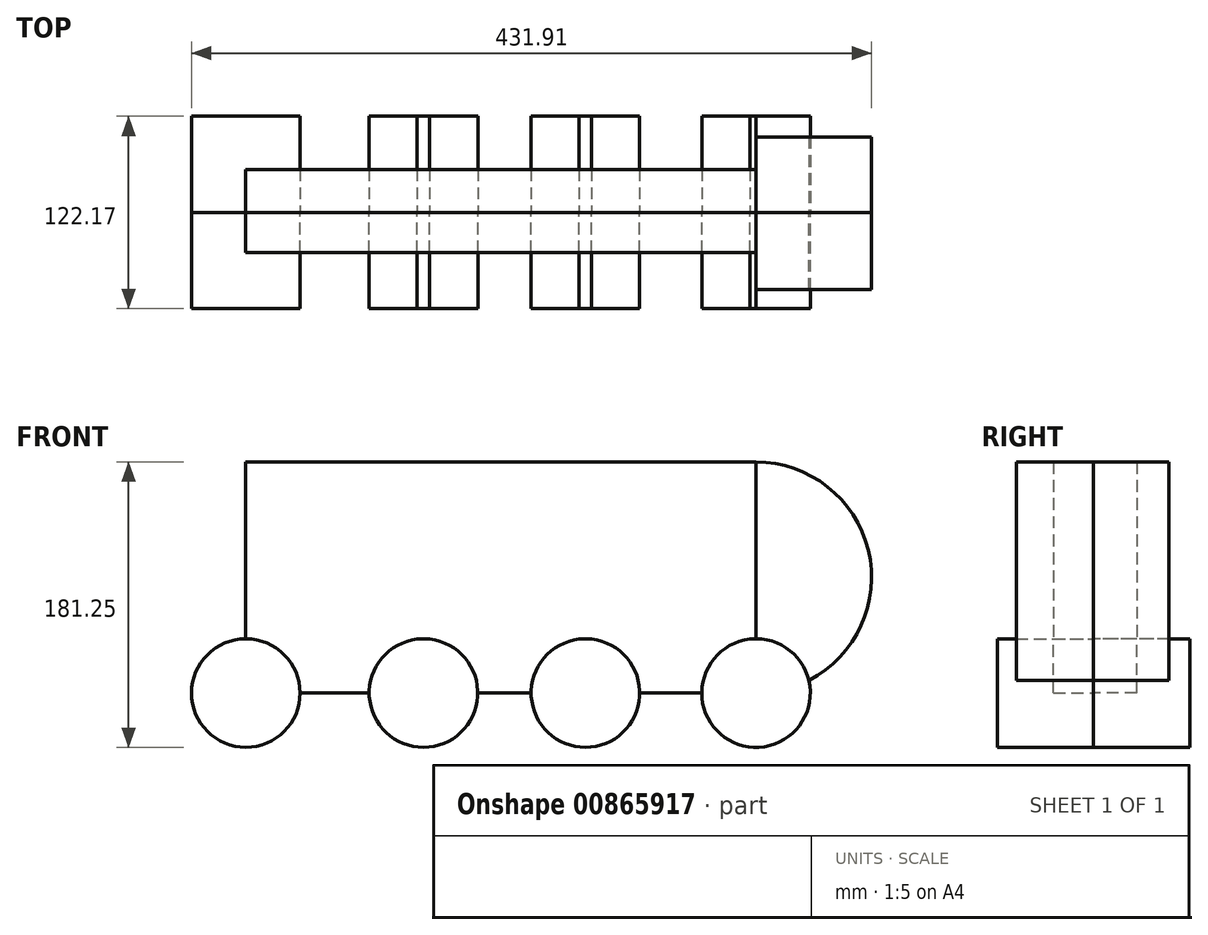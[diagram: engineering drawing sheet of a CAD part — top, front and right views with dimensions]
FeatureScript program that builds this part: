
annotation { "Feature Type Name" : "Feature", "Feature Type Description" : "" }
export const myFeature = defineFeature(function(context is Context, id is Id, definition is map)
    precondition{}
    {
        {
            var Q0;
            Q0=qCreatedBy(makeId("Front.planeOp"),FACE);
            var sketch = newSketch(context, id + "F0", { "sketchPlane" : qUnion([Q0])});
            skLineSegment(sketch, "E0.bottom", {"start": v(-75.86, 0) * mm, "end": v(211.2, 0) * mm});
            skLineSegment(sketch, "E0.top", {"start": v(-75.86, 34.24) * mm, "end": v(211.2, 34.24) * mm});
            skLineSegment(sketch, "E0.left", {"start": v(-75.86, 0) * mm, "end": v(-75.86, 34.24) * mm});
            skLineSegment(sketch, "E0.right", {"start": v(211.2, 0) * mm, "end": v(211.2, 34.24) * mm});
            skLineSegment(sketch, "E1.bottom", {"start": v(-75.86, 0) * mm, "end": v(-112.85, 0) * mm});
            skLineSegment(sketch, "E1.top", {"start": v(-75.86, 146.78) * mm, "end": v(-112.85, 146.78) * mm});
            skLineSegment(sketch, "E1.left", {"start": v(-75.86, 0) * mm, "end": v(-75.86, 146.78) * mm});
            skLineSegment(sketch, "E1.right", {"start": v(-112.85, 0) * mm, "end": v(-112.85, 146.78) * mm});
            skLineSegment(sketch, "E2.bottom", {"start": v(-75.86, 146.78) * mm, "end": v(211.2, 146.78) * mm});
            skLineSegment(sketch, "E2.top", {"start": v(-75.86, 112.91) * mm, "end": v(211.2, 112.91) * mm});
            skLineSegment(sketch, "E2.left", {"start": v(-75.86, 146.78) * mm, "end": v(-75.86, 112.91) * mm});
            skLineSegment(sketch, "E2.right", {"start": v(211.2, 146.78) * mm, "end": v(211.2, 112.91) * mm});
            skArc(sketch, "E3", {"start": v(211.2, 0) * mm, "mid": v(284.59, 73.39) * mm, "end": v(211.2, 146.78) * mm});
            skCircle(sketch, "E4", {"center": v(-112.85, 0) * mm, "radius": 34.47 * mm});
            skCircle(sketch, "E5", {"center": v(0, 0) * mm, "radius": 34.47 * mm});
            skCircle(sketch, "E6", {"center": v(211.2, 0) * mm, "radius": 34.47 * mm});
            skCircle(sketch, "E7", {"center": v(102.83, 0) * mm, "radius": 34.47 * mm});
            skLineSegment(sketch, "E8", {"start": v(211.2, 112.91) * mm, "end": v(211.2, 34.24) * mm});
            skSolve(sketch);
        }
        {
            var Q0;
            {var subQ0=sQuery(id+"F0.wireOp",EDGE,"E1.right");var subQ1=sQuery(id+"F0.wireOp",EDGE,"E1.bottom");var subQ2=makeQuery(id+"F0.imprint","INTERSECT",VERTEX,{"derivedFrom":[subQ1,subQ0]});Q0=makeQuery(id+"F0.imprint","IMPRINT",FACE,{"disambiguationData":[TD([[makeQuery(id+"F0.imprint","IMPRINT",EDGE,{"disambiguationData":[TD([[subQ2,1.0]])],"derivedFrom":subQ1}),1.0]])]});}
            var Q1;
            {var subQ0=sQuery(id+"F0.wireOp",EDGE,"E5");var subQ1=sQuery(id+"F0.wireOp",EDGE,"E0.bottom");var subQ2=makeQuery(id+"F0.imprint","INTERSECT",VERTEX,{"disambiguationData":[OD(0.0)],"derivedFrom":[subQ1,subQ0]});Q1=makeQuery(id+"F0.imprint","IMPRINT",FACE,{"disambiguationData":[TD([[makeQuery(id+"F0.imprint","IMPRINT",EDGE,{"disambiguationData":[TD([[subQ2,-1.0]])],"derivedFrom":subQ1}),-1.0]])]});}
            var Q2;
            {var subQ0=sQuery(id+"F0.wireOp",EDGE,"E7");var subQ1=sQuery(id+"F0.wireOp",EDGE,"E0.bottom");var subQ2=makeQuery(id+"F0.imprint","INTERSECT",VERTEX,{"disambiguationData":[OD(0.0)],"derivedFrom":[subQ1,subQ0]});Q2=makeQuery(id+"F0.imprint","IMPRINT",FACE,{"disambiguationData":[TD([[makeQuery(id+"F0.imprint","IMPRINT",EDGE,{"disambiguationData":[TD([[subQ2,-1.0]])],"derivedFrom":subQ1}),-1.0]])]});}
            var Q3;
            {var subQ1=sQuery(id+"F0.wireOp",EDGE,"E0.bottom");var subQ3=sQuery(id+"F0.wireOp",EDGE,"E6");var subQ4=makeQuery(id+"F0.imprint","INTERSECT",VERTEX,{"derivedFrom":[subQ1,subQ3]});Q3=makeQuery(id+"F0.imprint","IMPRINT",FACE,{"disambiguationData":[TD([[makeQuery(id+"F0.imprint","IMPRINT",EDGE,{"disambiguationData":[TD([[subQ4,-1.0]])],"derivedFrom":subQ3}),1.0]])]});}
            var Q4;
            {var subQ0=sQuery(id+"F0.wireOp",EDGE,"E0.right");Q4=makeQuery(id+"F0.imprint","IMPRINT",FACE,{"disambiguationData":[TD([[makeQuery(id+"F0.imprint","IMPRINT",EDGE,{"derivedFrom":subQ0}),1.0]])]});}
            var Q5;
            {var subQ0=sQuery(id+"F0.wireOp",EDGE,"E0.right");Q5=makeQuery(id+"F0.imprint","IMPRINT",FACE,{"disambiguationData":[TD([[makeQuery(id+"F0.imprint","IMPRINT",EDGE,{"derivedFrom":subQ0}),-1.0]])]});}
            var Q6;
            {var subQ0=sQuery(id+"F0.wireOp",EDGE,"E7");var subQ1=sQuery(id+"F0.wireOp",EDGE,"E0.bottom");var subQ2=makeQuery(id+"F0.imprint","INTERSECT",VERTEX,{"disambiguationData":[OD(0.0)],"derivedFrom":[subQ1,subQ0]});Q6=makeQuery(id+"F0.imprint","IMPRINT",FACE,{"disambiguationData":[TD([[makeQuery(id+"F0.imprint","IMPRINT",EDGE,{"disambiguationData":[TD([[subQ2,-1.0]])],"derivedFrom":subQ1}),1.0]])]});}
            var Q7;
            {var subQ0=sQuery(id+"F0.wireOp",EDGE,"E1.right");var subQ1=sQuery(id+"F0.wireOp",EDGE,"E1.bottom");var subQ2=makeQuery(id+"F0.imprint","INTERSECT",VERTEX,{"derivedFrom":[subQ1,subQ0]});Q7=makeQuery(id+"F0.imprint","IMPRINT",FACE,{"disambiguationData":[TD([[makeQuery(id+"F0.imprint","IMPRINT",EDGE,{"disambiguationData":[TD([[subQ2,1.0]])],"derivedFrom":subQ1}),-1.0]])]});}
            var Q8;
            {var subQ0=sQuery(id+"F0.wireOp",EDGE,"E5");var subQ1=sQuery(id+"F0.wireOp",EDGE,"E0.bottom");var subQ2=makeQuery(id+"F0.imprint","INTERSECT",VERTEX,{"disambiguationData":[OD(0.0)],"derivedFrom":[subQ1,subQ0]});Q8=makeQuery(id+"F0.imprint","IMPRINT",FACE,{"disambiguationData":[TD([[makeQuery(id+"F0.imprint","IMPRINT",EDGE,{"disambiguationData":[TD([[subQ2,-1.0]])],"derivedFrom":subQ1}),1.0]])]});}
            extrude(context, id + "F1", {"entities" : qUnion([Q0, Q1, Q2, Q3, Q4, Q5, Q6, Q7, Q8]), "depth" : 60.96 * mm, "offsetDistance" : 25.4 * mm});
        }
        {
            var Q0;
            {var subQ0=sQuery(id+"F0.wireOp",EDGE,"E1.right");var subQ1=sQuery(id+"F0.wireOp",EDGE,"E1.bottom");var subQ2=makeQuery(id+"F0.imprint","INTERSECT",VERTEX,{"derivedFrom":[subQ1,subQ0]});Q0=makeQuery(id+"F0.imprint","IMPRINT",FACE,{"disambiguationData":[TD([[makeQuery(id+"F0.imprint","IMPRINT",EDGE,{"disambiguationData":[TD([[subQ2,1.0]])],"derivedFrom":subQ1}),1.0]])]});}
            var Q1;
            {var subQ0=sQuery(id+"F0.wireOp",EDGE,"E1.right");var subQ1=sQuery(id+"F0.wireOp",EDGE,"E1.bottom");var subQ2=makeQuery(id+"F0.imprint","INTERSECT",VERTEX,{"derivedFrom":[subQ1,subQ0]});Q1=makeQuery(id+"F0.imprint","IMPRINT",FACE,{"disambiguationData":[TD([[makeQuery(id+"F0.imprint","IMPRINT",EDGE,{"disambiguationData":[TD([[subQ2,1.0]])],"derivedFrom":subQ1}),-1.0]])]});}
            var Q2;
            {var subQ0=sQuery(id+"F0.wireOp",EDGE,"E5");var subQ1=sQuery(id+"F0.wireOp",EDGE,"E0.bottom");var subQ2=makeQuery(id+"F0.imprint","INTERSECT",VERTEX,{"disambiguationData":[OD(0.0)],"derivedFrom":[subQ1,subQ0]});Q2=makeQuery(id+"F0.imprint","IMPRINT",FACE,{"disambiguationData":[TD([[makeQuery(id+"F0.imprint","IMPRINT",EDGE,{"disambiguationData":[TD([[subQ2,-1.0]])],"derivedFrom":subQ1}),-1.0]])]});}
            var Q3;
            {var subQ0=sQuery(id+"F0.wireOp",EDGE,"E5");var subQ1=sQuery(id+"F0.wireOp",EDGE,"E0.bottom");var subQ2=makeQuery(id+"F0.imprint","INTERSECT",VERTEX,{"disambiguationData":[OD(0.0)],"derivedFrom":[subQ1,subQ0]});Q3=makeQuery(id+"F0.imprint","IMPRINT",FACE,{"disambiguationData":[TD([[makeQuery(id+"F0.imprint","IMPRINT",EDGE,{"disambiguationData":[TD([[subQ2,-1.0]])],"derivedFrom":subQ1}),1.0]])]});}
            var Q4;
            {var subQ0=sQuery(id+"F0.wireOp",EDGE,"E7");var subQ1=sQuery(id+"F0.wireOp",EDGE,"E0.bottom");var subQ2=makeQuery(id+"F0.imprint","INTERSECT",VERTEX,{"disambiguationData":[OD(0.0)],"derivedFrom":[subQ1,subQ0]});Q4=makeQuery(id+"F0.imprint","IMPRINT",FACE,{"disambiguationData":[TD([[makeQuery(id+"F0.imprint","IMPRINT",EDGE,{"disambiguationData":[TD([[subQ2,-1.0]])],"derivedFrom":subQ1}),1.0]])]});}
            var Q5;
            {var subQ0=sQuery(id+"F0.wireOp",EDGE,"E7");var subQ1=sQuery(id+"F0.wireOp",EDGE,"E0.bottom");var subQ2=makeQuery(id+"F0.imprint","INTERSECT",VERTEX,{"disambiguationData":[OD(0.0)],"derivedFrom":[subQ1,subQ0]});Q5=makeQuery(id+"F0.imprint","IMPRINT",FACE,{"disambiguationData":[TD([[makeQuery(id+"F0.imprint","IMPRINT",EDGE,{"disambiguationData":[TD([[subQ2,-1.0]])],"derivedFrom":subQ1}),-1.0]])]});}
            var Q6;
            {var subQ0=sQuery(id+"F0.wireOp",EDGE,"E0.right");Q6=makeQuery(id+"F0.imprint","IMPRINT",FACE,{"disambiguationData":[TD([[makeQuery(id+"F0.imprint","IMPRINT",EDGE,{"derivedFrom":subQ0}),1.0]])]});}
            var Q7;
            {var subQ0=sQuery(id+"F0.wireOp",EDGE,"E0.right");Q7=makeQuery(id+"F0.imprint","IMPRINT",FACE,{"disambiguationData":[TD([[makeQuery(id+"F0.imprint","IMPRINT",EDGE,{"derivedFrom":subQ0}),-1.0]])]});}
            var Q8;
            {var subQ1=sQuery(id+"F0.wireOp",EDGE,"E0.bottom");var subQ3=sQuery(id+"F0.wireOp",EDGE,"E6");var subQ4=makeQuery(id+"F0.imprint","INTERSECT",VERTEX,{"derivedFrom":[subQ1,subQ3]});Q8=makeQuery(id+"F0.imprint","IMPRINT",FACE,{"disambiguationData":[TD([[makeQuery(id+"F0.imprint","IMPRINT",EDGE,{"disambiguationData":[TD([[subQ4,-1.0]])],"derivedFrom":subQ3}),1.0]])]});}
            extrude(context, id + "F2", {"entities" : qUnion([Q0, Q1, Q2, Q3, Q4, Q5, Q6, Q7, Q8]), "oppositeDirection" : true, "depth" : 61.2 * mm, "offsetDistance" : 25.4 * mm});
        }
        {
            var Q0;
            {var subQ5=sQuery(id+"F0.wireOp",EDGE,"E1.top");Q0=makeQuery(id+"F0.imprint","IMPRINT",FACE,{"disambiguationData":[TD([[makeQuery(id+"F0.imprint","IMPRINT",EDGE,{"derivedFrom":subQ5}),1.0]])]});}
            var Q1;
            {var subQ0=sQuery(id+"F0.wireOp",EDGE,"E1.left");var subQ5=sQuery(id+"F0.wireOp",EDGE,"E0.top");var subQ7=makeQuery(id+"F0.imprint","INTERSECT",VERTEX,{"derivedFrom":[subQ5,subQ0]});Q1=makeQuery(id+"F0.imprint","IMPRINT",FACE,{"disambiguationData":[TD([[makeQuery(id+"F0.imprint","IMPRINT",EDGE,{"disambiguationData":[TD([[subQ7,-1.0]])],"derivedFrom":subQ5}),-1.0]])]});}
            var Q2;
            {var subQ0=sQuery(id+"F0.wireOp",EDGE,"E5");var subQ1=sQuery(id+"F0.wireOp",EDGE,"E0.bottom");var subQ2=makeQuery(id+"F0.imprint","INTERSECT",VERTEX,{"disambiguationData":[OD(1.0)],"derivedFrom":[subQ1,subQ0]});Q2=makeQuery(id+"F0.imprint","IMPRINT",FACE,{"disambiguationData":[TD([[makeQuery(id+"F0.imprint","IMPRINT",EDGE,{"disambiguationData":[TD([[subQ2,-1.0]])],"derivedFrom":subQ1}),1.0]])]});}
            var Q3;
            {var subQ0=sQuery(id+"F0.wireOp",EDGE,"E7");var subQ1=sQuery(id+"F0.wireOp",EDGE,"E0.bottom");var subQ2=makeQuery(id+"F0.imprint","INTERSECT",VERTEX,{"disambiguationData":[OD(1.0)],"derivedFrom":[subQ1,subQ0]});Q3=makeQuery(id+"F0.imprint","IMPRINT",FACE,{"disambiguationData":[TD([[makeQuery(id+"F0.imprint","IMPRINT",EDGE,{"disambiguationData":[TD([[subQ2,-1.0]])],"derivedFrom":subQ1}),1.0]])]});}
            var Q4;
            Q4=makeQuery(id+"F0.imprint","IMPRINT",FACE,{"disambiguationData":[TD([[makeQuery(id+"F0.imprint","IMPRINT",EDGE,{"derivedFrom":sQuery(id+"F0.wireOp",EDGE,"E2.bottom")}),-1.0]])]});
            var Q5;
            {var subQ3=sQuery(id+"F0.wireOp",EDGE,"E2.top");Q5=makeQuery(id+"F0.imprint","IMPRINT",FACE,{"disambiguationData":[TD([[makeQuery(id+"F0.imprint","IMPRINT",EDGE,{"derivedFrom":subQ3}),-1.0]])]});}
            extrude(context, id + "F3", {"entities" : qUnion([Q0, Q1, Q2, Q3, Q4, Q5]), "depth" : 25.4 * mm, "offsetDistance" : 25.4 * mm});
        }
        {
            var Q0;
            {var subQ5=sQuery(id+"F0.wireOp",EDGE,"E1.top");Q0=makeQuery(id+"F0.imprint","IMPRINT",FACE,{"disambiguationData":[TD([[makeQuery(id+"F0.imprint","IMPRINT",EDGE,{"derivedFrom":subQ5}),1.0]])]});}
            var Q1;
            {var subQ0=sQuery(id+"F0.wireOp",EDGE,"E1.left");var subQ5=sQuery(id+"F0.wireOp",EDGE,"E0.top");var subQ7=makeQuery(id+"F0.imprint","INTERSECT",VERTEX,{"derivedFrom":[subQ5,subQ0]});Q1=makeQuery(id+"F0.imprint","IMPRINT",FACE,{"disambiguationData":[TD([[makeQuery(id+"F0.imprint","IMPRINT",EDGE,{"disambiguationData":[TD([[subQ7,-1.0]])],"derivedFrom":subQ5}),-1.0]])]});}
            var Q2;
            {var subQ0=sQuery(id+"F0.wireOp",EDGE,"E5");var subQ1=sQuery(id+"F0.wireOp",EDGE,"E0.bottom");var subQ2=makeQuery(id+"F0.imprint","INTERSECT",VERTEX,{"disambiguationData":[OD(1.0)],"derivedFrom":[subQ1,subQ0]});Q2=makeQuery(id+"F0.imprint","IMPRINT",FACE,{"disambiguationData":[TD([[makeQuery(id+"F0.imprint","IMPRINT",EDGE,{"disambiguationData":[TD([[subQ2,-1.0]])],"derivedFrom":subQ1}),1.0]])]});}
            var Q3;
            {var subQ0=sQuery(id+"F0.wireOp",EDGE,"E7");var subQ1=sQuery(id+"F0.wireOp",EDGE,"E0.bottom");var subQ2=makeQuery(id+"F0.imprint","INTERSECT",VERTEX,{"disambiguationData":[OD(1.0)],"derivedFrom":[subQ1,subQ0]});Q3=makeQuery(id+"F0.imprint","IMPRINT",FACE,{"disambiguationData":[TD([[makeQuery(id+"F0.imprint","IMPRINT",EDGE,{"disambiguationData":[TD([[subQ2,-1.0]])],"derivedFrom":subQ1}),1.0]])]});}
            var Q4;
            {var subQ3=sQuery(id+"F0.wireOp",EDGE,"E2.top");Q4=makeQuery(id+"F0.imprint","IMPRINT",FACE,{"disambiguationData":[TD([[makeQuery(id+"F0.imprint","IMPRINT",EDGE,{"derivedFrom":subQ3}),-1.0]])]});}
            var Q5;
            Q5=makeQuery(id+"F0.imprint","IMPRINT",FACE,{"disambiguationData":[TD([[makeQuery(id+"F0.imprint","IMPRINT",EDGE,{"derivedFrom":sQuery(id+"F0.wireOp",EDGE,"E2.bottom")}),-1.0]])]});
            extrude(context, id + "F4", {"entities" : qUnion([Q0, Q1, Q2, Q3, Q4, Q5]), "oppositeDirection" : true, "depth" : 27.43 * mm, "offsetDistance" : 25.4 * mm});
        }
        {
            var Q0;
            {var subQ0=sQuery(id+"F0.wireOp",EDGE,"E2.right");Q0=makeQuery(id+"F0.imprint","IMPRINT",FACE,{"disambiguationData":[TD([[makeQuery(id+"F0.imprint","IMPRINT",EDGE,{"derivedFrom":subQ0}),1.0]])]});}
            extrude(context, id + "F5", {"entities" : qUnion([Q0]), "depth" : 49.02 * mm, "offsetDistance" : 25.4 * mm});
        }
        {
            var Q0;
            {var subQ0=sQuery(id+"F0.wireOp",EDGE,"E2.right");Q0=makeQuery(id+"F0.imprint","IMPRINT",FACE,{"disambiguationData":[TD([[makeQuery(id+"F0.imprint","IMPRINT",EDGE,{"derivedFrom":subQ0}),1.0]])]});}
            extrude(context, id + "F6", {"entities" : qUnion([Q0]), "oppositeDirection" : true, "depth" : 48 * mm, "offsetDistance" : 25.4 * mm});
        }
    });
